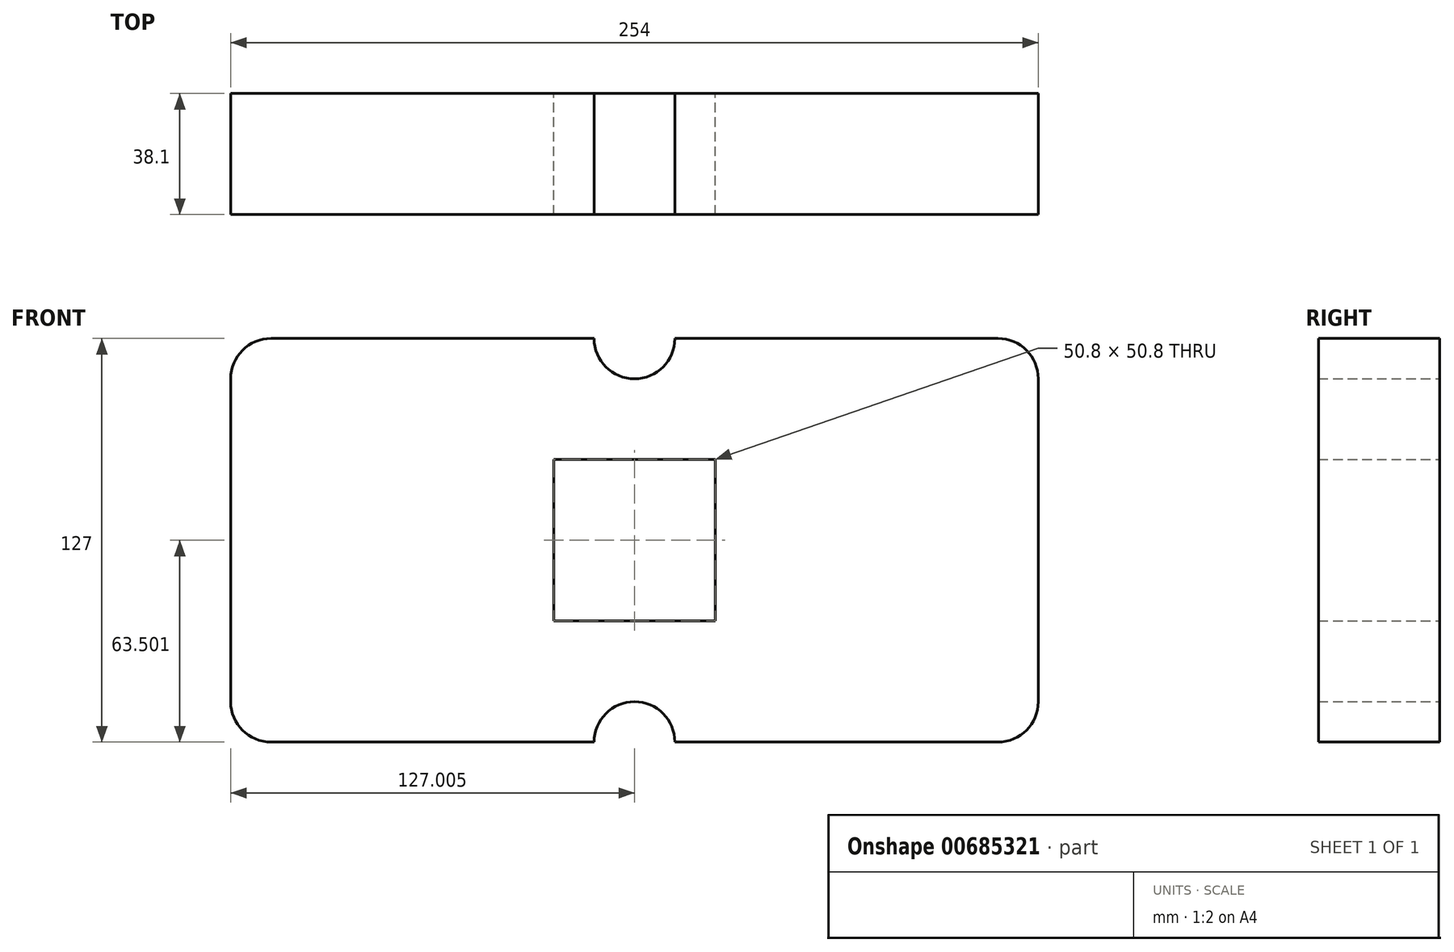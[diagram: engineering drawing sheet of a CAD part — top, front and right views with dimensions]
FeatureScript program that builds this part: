
annotation { "Feature Type Name" : "Feature", "Feature Type Description" : "" }
export const myFeature = defineFeature(function(context is Context, id is Id, definition is map)
    precondition{}
    {
        {
            var Q0;
            Q0=qCreatedBy(makeId("Front.planeOp"),FACE);
            var sketch = newSketch(context, id + "F0", { "sketchPlane" : qUnion([Q0])});
            skLineSegment(sketch, "E0.bottom", {"start": v(-112.96, 56.95) * mm, "end": v(-11.36, 56.95) * mm});
            skLineSegment(sketch, "E0.top", {"start": v(-112.96, -70.05) * mm, "end": v(-11.36, -70.05) * mm});
            skLineSegment(sketch, "E0.left", {"start": v(-125.66, 44.25) * mm, "end": v(-125.66, -57.35) * mm});
            skLineSegment(sketch, "E0.right", {"start": v(128.34, 44.25) * mm, "end": v(128.34, -57.35) * mm});
            skPoint(sketch, "E1.visualSharp", {"position": v(-125.66, 56.95) * mm});
            skArc(sketch, "E1.filletArc", {"start": v(-112.96, 56.95) * mm, "mid": v(-121.94, 53.23) * mm, "end": v(-125.66, 44.25) * mm});
            skPoint(sketch, "E2.visualSharp", {"position": v(-125.66, -70.05) * mm});
            skArc(sketch, "E2.filletArc", {"start": v(-125.66, -57.35) * mm, "mid": v(-121.94, -66.33) * mm, "end": v(-112.96, -70.05) * mm});
            skPoint(sketch, "E3.visualSharp", {"position": v(128.34, -70.05) * mm});
            skArc(sketch, "E3.filletArc", {"start": v(115.64, -70.05) * mm, "mid": v(124.62, -66.33) * mm, "end": v(128.34, -57.35) * mm});
            skPoint(sketch, "E4.visualSharp", {"position": v(128.34, 56.95) * mm});
            skArc(sketch, "E4.filletArc", {"start": v(128.34, 44.25) * mm, "mid": v(124.62, 53.23) * mm, "end": v(115.64, 56.95) * mm});
            skArc(sketch, "E5", {"start": v(-11.36, 56.95) * mm, "mid": v(1.34, 44.25) * mm, "end": v(14.04, 56.95) * mm});
            skArc(sketch, "E6", {"start": v(14.04, -70.05) * mm, "mid": v(1.34, -57.35) * mm, "end": v(-11.36, -70.05) * mm});
            skLineSegment(sketch, "E7.trimOffspring", {"start": v(14.04, 56.95) * mm, "end": v(115.64, 56.95) * mm});
            skLineSegment(sketch, "E8.trimOffspring", {"start": v(14.04, -70.05) * mm, "end": v(115.64, -70.05) * mm});
            skLineSegment(sketch, "E9", {"start": v(-24.06, -31.95) * mm, "end": v(26.74, -31.95) * mm});
            skLineSegment(sketch, "E10", {"start": v(26.74, -31.95) * mm, "end": v(26.74, 18.85) * mm});
            skLineSegment(sketch, "E11", {"start": v(26.74, 18.85) * mm, "end": v(-24.06, 18.85) * mm});
            skLineSegment(sketch, "E12", {"start": v(-24.06, 18.85) * mm, "end": v(-24.06, -31.95) * mm});
            skSolve(sketch);
        }
        {
            var Q0;
            Q0 = qSketchRegion(id + "F0", true);
            extrude(context, id + "F1", {"entities" : qUnion([Q0]), "depth" : 38.1 * mm, "offsetDistance" : 25.4 * mm});
        }
    });
